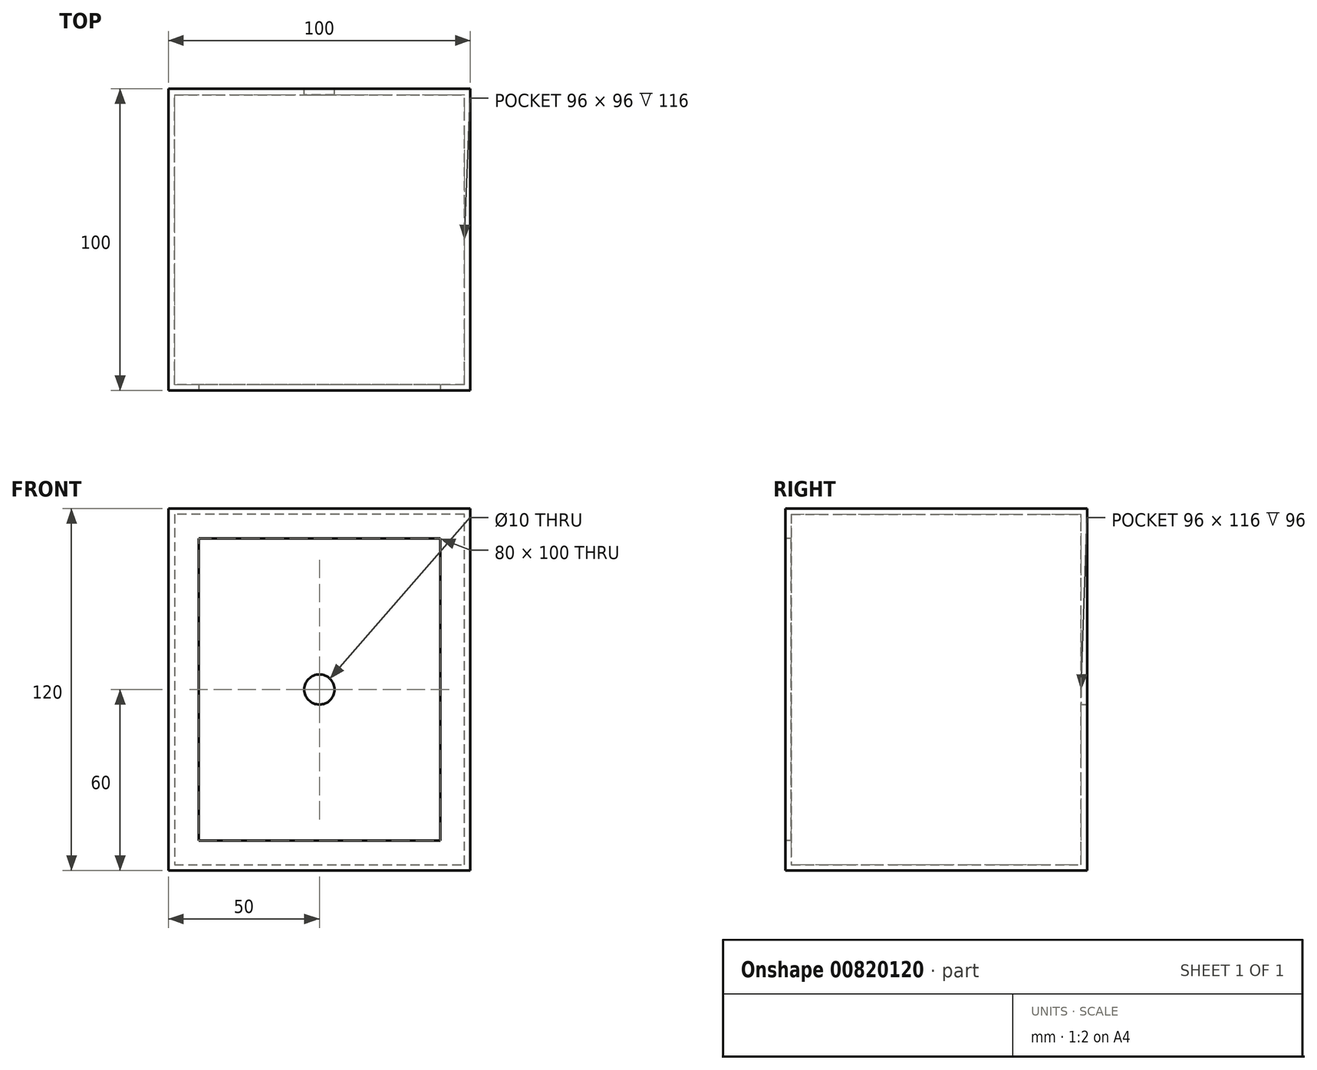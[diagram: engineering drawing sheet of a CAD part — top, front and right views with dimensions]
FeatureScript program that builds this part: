
annotation { "Feature Type Name" : "Feature", "Feature Type Description" : "" }
export const myFeature = defineFeature(function(context is Context, id is Id, definition is map)
    precondition{}
    {
        {
            var Q0;
            Q0=qCreatedBy(makeId("Front.planeOp"),FACE);
            var sketch = newSketch(context, id + "F0", { "sketchPlane" : qUnion([Q0])});
            skLineSegment(sketch, "E0", {"start": v(50, 0) * mm, "end": v(50, 60) * mm});
            skLineSegment(sketch, "E1", {"start": v(50, 60) * mm, "end": v(-50, 60) * mm});
            skLineSegment(sketch, "E2", {"start": v(-50, 60) * mm, "end": v(-50, -60) * mm});
            skLineSegment(sketch, "E3", {"start": v(-50, -60) * mm, "end": v(50, -60) * mm});
            skLineSegment(sketch, "E4", {"start": v(50, -60) * mm, "end": v(50, 0) * mm});
            skLineSegment(sketch, "E5.0", {"start": v(-48, 58) * mm, "end": v(-48, -58) * mm});
            skLineSegment(sketch, "E6.0", {"start": v(48, 58) * mm, "end": v(-48, 58) * mm});
            skLineSegment(sketch, "E7.0", {"start": v(48, 0) * mm, "end": v(48, 58) * mm});
            skLineSegment(sketch, "E8.0", {"start": v(48, -58) * mm, "end": v(48, 0) * mm});
            skLineSegment(sketch, "E9.0", {"start": v(-48, -58) * mm, "end": v(48, -58) * mm});
            skSolve(sketch);
        }
        {
            var Q0;
            Q0=makeQuery(id+"F0.imprint","IMPRINT",FACE,{"disambiguationData":[TD([[makeQuery(id+"F0.imprint","IMPRINT",EDGE,{"derivedFrom":sQuery(id+"F0.wireOp",EDGE,"E0")}),1.0]])]});
            extrude(context, id + "F1", {"entities" : qUnion([Q0]), "endBound" : BoundingType.SYMMETRIC, "depth" : 100 * mm, "offsetDistance" : 25 * mm});
        }
        {
            var Q0;
            Q0=makeQuery(id+"F1.opExtrude","CAP_FACE",FACE,{"disambiguationData":[OSD([sQuery(id+"F0.wireOp",EDGE,"E0"),sQuery(id+"F0.wireOp",EDGE,"E1"),sQuery(id+"F0.wireOp",EDGE,"E2"),sQuery(id+"F0.wireOp",EDGE,"E3"),sQuery(id+"F0.wireOp",EDGE,"E4"),sQuery(id+"F0.wireOp",EDGE,"E5.0"),sQuery(id+"F0.wireOp",EDGE,"E6.0"),sQuery(id+"F0.wireOp",EDGE,"E7.0"),sQuery(id+"F0.wireOp",EDGE,"E8.0"),sQuery(id+"F0.wireOp",EDGE,"E9.0")])],"isStart":true});
            var sketch = newSketch(context, id + "F2", { "sketchPlane" : qUnion([Q0])});
            skLineSegment(sketch, "E10", {"start": v(-50, 60) * mm, "end": v(50, 60) * mm});
            skLineSegment(sketch, "E11", {"start": v(50, 60) * mm, "end": v(50, -60) * mm});
            skLineSegment(sketch, "E12", {"start": v(50, -60) * mm, "end": v(-50, -60) * mm});
            skLineSegment(sketch, "E13", {"start": v(-50, -60) * mm, "end": v(-50, 60) * mm});
            skSolve(sketch);
        }
        {
            var Q0;
            Q0 = qSketchRegion(id + "F2", true);
            extrude(context, id + "F3", {"entities" : qUnion([Q0]), "operationType" : NewBodyOperationType.ADD, "oppositeDirection" : true, "depth" : 2 * mm, "offsetDistance" : 25 * mm});
        }
        {
            var Q0;
            Q0=makeQuery(id+"F3.boolean.opBoolean","MERGE",FACE,{"derivedFrom":[makeQuery(id+"F1.opExtrude","CAP_FACE",FACE,{"disambiguationData":[OSD([sQuery(id+"F0.wireOp",EDGE,"E0"),sQuery(id+"F0.wireOp",EDGE,"E1"),sQuery(id+"F0.wireOp",EDGE,"E2"),sQuery(id+"F0.wireOp",EDGE,"E3"),sQuery(id+"F0.wireOp",EDGE,"E4"),sQuery(id+"F0.wireOp",EDGE,"E5.0"),sQuery(id+"F0.wireOp",EDGE,"E6.0"),sQuery(id+"F0.wireOp",EDGE,"E7.0"),sQuery(id+"F0.wireOp",EDGE,"E8.0"),sQuery(id+"F0.wireOp",EDGE,"E9.0")])],"isStart":true}),makeQuery(id+"F3.opExtrude","CAP_FACE",FACE,{"disambiguationData":[OSD([sQuery(id+"F2.wireOp",EDGE,"E10"),sQuery(id+"F2.wireOp",EDGE,"E11"),sQuery(id+"F2.wireOp",EDGE,"E12"),sQuery(id+"F2.wireOp",EDGE,"E13")])],"isStart":true})]});
            var sketch = newSketch(context, id + "F4", { "sketchPlane" : qUnion([Q0])});
            skLineSegment(sketch, "E14", {"start": v(-50, 0) * mm, "end": v(0, 0) * mm});
            skSolve(sketch);
        }
        {
            var Q0;
            Q0=sQuery(id+"F4.wireOp",VERTEX,"E14.end");
            var Q1;
            Q1=makeQuery(id+"F1.opExtrude","SWEPT_BODY",BODY,{"disambiguationData":[OSD([sQuery(id+"F0.wireOp",EDGE,"E0"),sQuery(id+"F0.wireOp",EDGE,"E1"),sQuery(id+"F0.wireOp",EDGE,"E2"),sQuery(id+"F0.wireOp",EDGE,"E3"),sQuery(id+"F0.wireOp",EDGE,"E4"),sQuery(id+"F0.wireOp",EDGE,"E5.0"),sQuery(id+"F0.wireOp",EDGE,"E6.0"),sQuery(id+"F0.wireOp",EDGE,"E7.0"),sQuery(id+"F0.wireOp",EDGE,"E8.0"),sQuery(id+"F0.wireOp",EDGE,"E9.0")])]});
            hole(context, id + "F5", {"style" : HoleStyle.SIMPLE, "endStyle" : HoleEndStyle.THROUGH, "holeDiameter" : 10 * mm, "majorDiameter" : 5 * mm, "isTappedThrough" : true, "tappedDepth" : 2.9 * mm, "tapClearance" : 3, "startFromSketch" : true, "locations" : qUnion([Q0]), "scope" : qUnion([Q1])});
        }
        {
            var Q0;
            Q0=makeQuery(id+"F1.opExtrude","CAP_FACE",FACE,{"disambiguationData":[OSD([sQuery(id+"F0.wireOp",EDGE,"E0"),sQuery(id+"F0.wireOp",EDGE,"E1"),sQuery(id+"F0.wireOp",EDGE,"E2"),sQuery(id+"F0.wireOp",EDGE,"E3"),sQuery(id+"F0.wireOp",EDGE,"E4"),sQuery(id+"F0.wireOp",EDGE,"E5.0"),sQuery(id+"F0.wireOp",EDGE,"E6.0"),sQuery(id+"F0.wireOp",EDGE,"E7.0"),sQuery(id+"F0.wireOp",EDGE,"E8.0"),sQuery(id+"F0.wireOp",EDGE,"E9.0")])],"isStart":false});
            var sketch = newSketch(context, id + "F6", { "sketchPlane" : qUnion([Q0])});
            skLineSegment(sketch, "E15", {"start": v(50, 60) * mm, "end": v(50, 55) * mm});
            skLineSegment(sketch, "E16", {"start": v(50, 60) * mm, "end": v(-50, 60) * mm});
            skLineSegment(sketch, "E17", {"start": v(-50, 60) * mm, "end": v(-50, -60) * mm});
            skLineSegment(sketch, "E18", {"start": v(-50, -60) * mm, "end": v(50, -60) * mm});
            skLineSegment(sketch, "E19", {"start": v(50, -60) * mm, "end": v(50, 55) * mm});
            skLineSegment(sketch, "E20.0", {"start": v(40, 50) * mm, "end": v(-40, 50) * mm});
            skLineSegment(sketch, "E21.0", {"start": v(-40, 50) * mm, "end": v(-40, -50) * mm});
            skLineSegment(sketch, "E22.0", {"start": v(-40, -50) * mm, "end": v(40, -50) * mm});
            skLineSegment(sketch, "E23.0", {"start": v(40, -50) * mm, "end": v(40, 50) * mm});
            skSolve(sketch);
        }
        {
            var Q0;
            Q0 = qSketchRegion(id + "F6", true);
            extrude(context, id + "F7", {"entities" : qUnion([Q0]), "operationType" : NewBodyOperationType.ADD, "oppositeDirection" : true, "depth" : 2 * mm, "offsetDistance" : 25 * mm});
        }
    });
